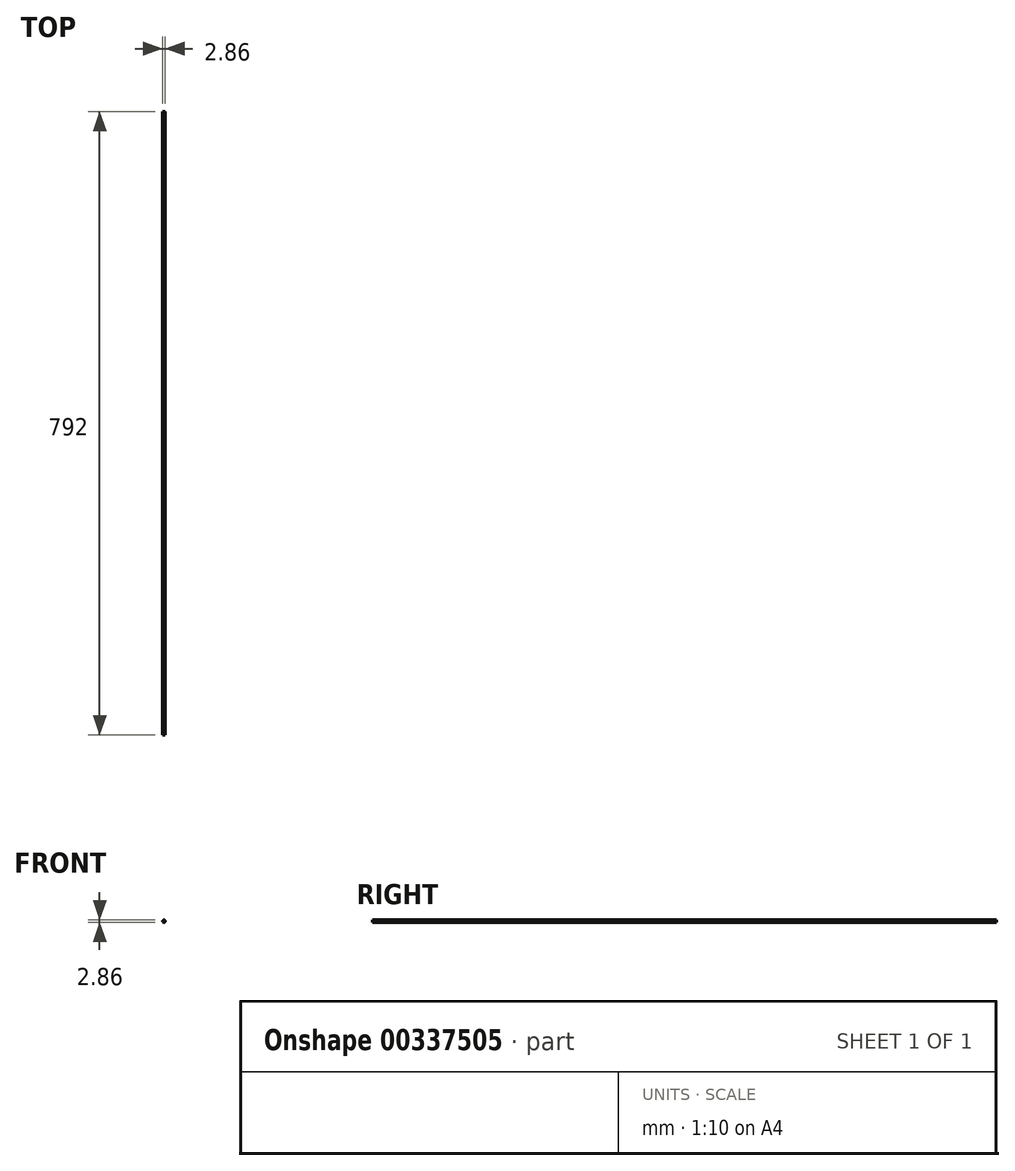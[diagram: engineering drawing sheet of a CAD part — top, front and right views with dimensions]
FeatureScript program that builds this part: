
annotation { "Feature Type Name" : "Feature", "Feature Type Description" : "" }
export const myFeature = defineFeature(function(context is Context, id is Id, definition is map)
    precondition{}
    {
        {
            var Q0;
            Q0=qCreatedBy(makeId("Front.planeOp"),FACE);
            var sketch = newSketch(context, id + "F0", { "sketchPlane" : qUnion([Q0])});
            skCircle(sketch, "E0", {"center": v(17.85, -17.77) * mm, "radius": 1.43 * mm});
            skSolve(sketch);
        }
        {
            var Q0;
            Q0 = qSketchRegion(id + "F0", true);
            extrude(context, id + "F1", {"entities" : qUnion([Q0]), "depth" : 792 * mm});
        }
    });
